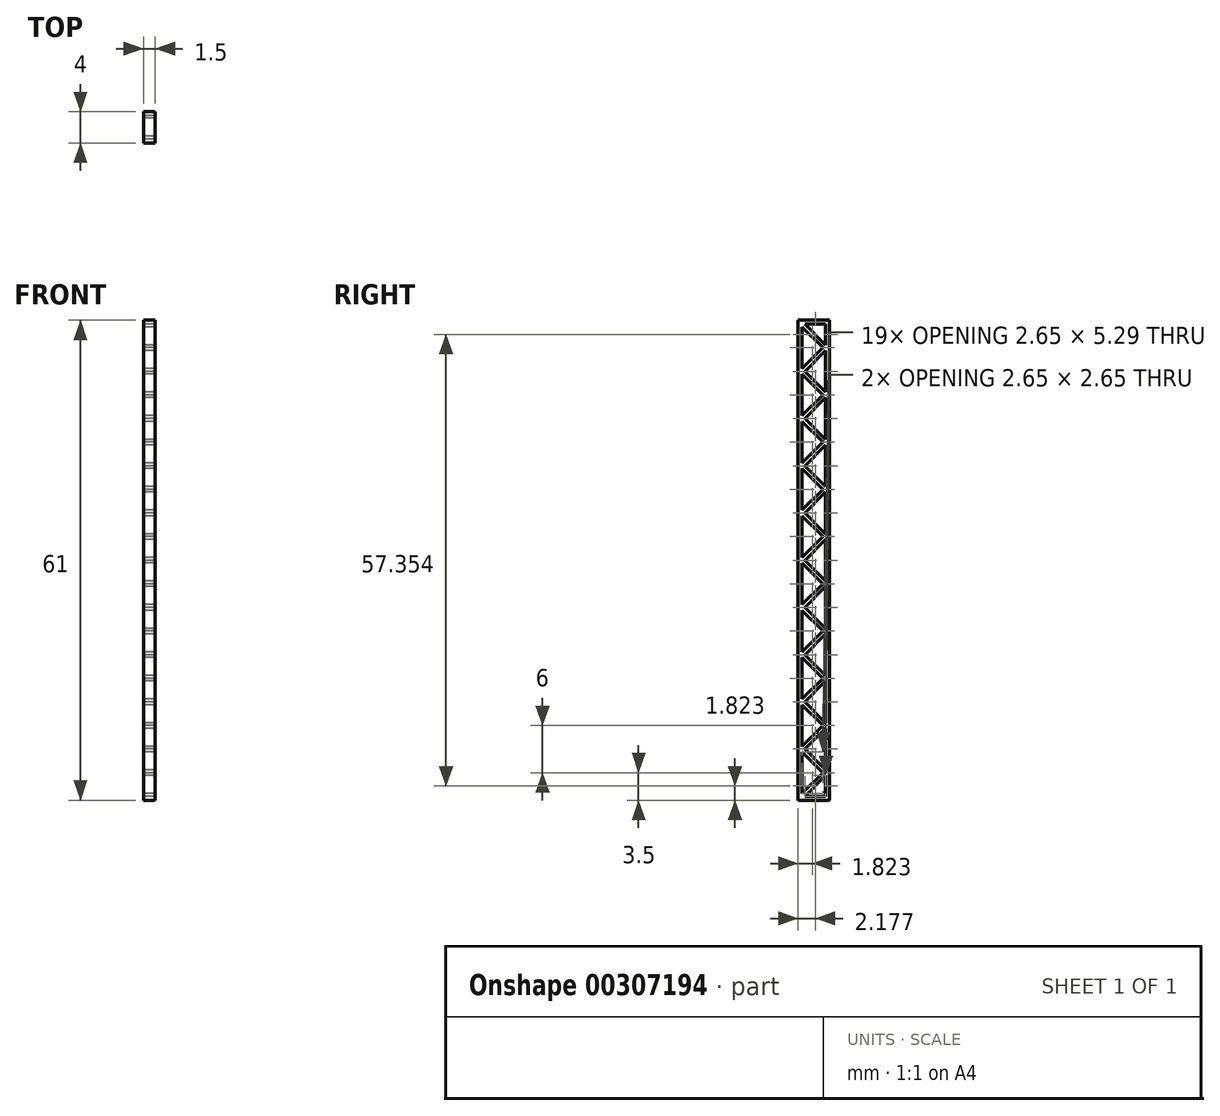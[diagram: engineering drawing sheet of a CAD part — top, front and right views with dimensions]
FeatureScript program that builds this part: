
annotation { "Feature Type Name" : "Feature", "Feature Type Description" : "" }
export const myFeature = defineFeature(function(context is Context, id is Id, definition is map)
    precondition{}
    {
        {
            var Q0;
            Q0=qCreatedBy(makeId("Right.planeOp"),FACE);
            var sketch = newSketch(context, id + "F0", { "sketchPlane" : qUnion([Q0])});
            skLineSegment(sketch, "E0.bottom", {"start": v(0, 0) * mm, "end": v(4, 0) * mm});
            skLineSegment(sketch, "E0.left", {"start": v(0, 0) * mm, "end": v(0, -60) * mm});
            skLineSegment(sketch, "E0.right", {"start": v(4, 0) * mm, "end": v(4, -60) * mm});
            skLineSegment(sketch, "E1.0", {"start": v(3.5, -0.5) * mm, "end": v(3.5, -3.15) * mm});
            skLineSegment(sketch, "E1.1", {"start": v(0.85, -0.5) * mm, "end": v(3.5, -0.5) * mm});
            skLineSegment(sketch, "E1.2", {"start": v(0.5, -0.85) * mm, "end": v(0.5, -6.15) * mm});
            skLineSegment(sketch, "E2.0", {"start": v(0.5, -0.85) * mm, "end": v(3.15, -3.5) * mm});
            skLineSegment(sketch, "E3.0", {"start": v(0.85, -0.5) * mm, "end": v(3.5, -3.15) * mm});
            skLineSegment(sketch, "E4.trimOffspring", {"start": v(3.5, -3.85) * mm, "end": v(3.5, -9.15) * mm});
            skLineSegment(sketch, "E5", {"start": v(3.15, -3.5) * mm, "end": v(0.5, -6.15) * mm});
            skLineSegment(sketch, "E6", {"start": v(0.85, -6.5) * mm, "end": v(3.5, -9.15) * mm});
            skLineSegment(sketch, "E7", {"start": v(3.15, -9.5) * mm, "end": v(0.5, -12.15) * mm});
            skLineSegment(sketch, "E8", {"start": v(0.85, -12.5) * mm, "end": v(3.5, -15.15) * mm});
            skLineSegment(sketch, "E9", {"start": v(3.15, -15.5) * mm, "end": v(0.5, -18.15) * mm});
            skLineSegment(sketch, "E10", {"start": v(0.85, -18.5) * mm, "end": v(3.5, -21.15) * mm});
            skLineSegment(sketch, "E11", {"start": v(3.15, -21.5) * mm, "end": v(0.5, -24.15) * mm});
            skLineSegment(sketch, "E12", {"start": v(0.85, -24.5) * mm, "end": v(3.5, -27.15) * mm});
            skLineSegment(sketch, "E13", {"start": v(3.15, -27.5) * mm, "end": v(0.5, -30.15) * mm});
            skLineSegment(sketch, "E14", {"start": v(0.85, -30.5) * mm, "end": v(3.5, -33.15) * mm});
            skLineSegment(sketch, "E15", {"start": v(3.15, -33.5) * mm, "end": v(0.5, -36.15) * mm});
            skLineSegment(sketch, "E16", {"start": v(0.85, -36.5) * mm, "end": v(3.5, -39.15) * mm});
            skLineSegment(sketch, "E17", {"start": v(3.15, -39.5) * mm, "end": v(0.5, -42.15) * mm});
            skLineSegment(sketch, "E18", {"start": v(0.85, -42.5) * mm, "end": v(3.5, -45.15) * mm});
            skLineSegment(sketch, "E19", {"start": v(3.15, -45.5) * mm, "end": v(0.5, -48.15) * mm});
            skLineSegment(sketch, "E20", {"start": v(0.85, -48.5) * mm, "end": v(3.5, -51.15) * mm});
            skLineSegment(sketch, "E21", {"start": v(3.15, -51.5) * mm, "end": v(0.5, -54.15) * mm});
            skLineSegment(sketch, "E22", {"start": v(0.85, -54.5) * mm, "end": v(3.5, -57.15) * mm});
            skLineSegment(sketch, "E23", {"start": v(3.15, -57.5) * mm, "end": v(0.5, -60.15) * mm});
            skLineSegment(sketch, "E24", {"start": v(3.5, -3.85) * mm, "end": v(0.85, -6.5) * mm});
            skLineSegment(sketch, "E25", {"start": v(0.5, -6.85) * mm, "end": v(3.15, -9.5) * mm});
            skLineSegment(sketch, "E26", {"start": v(3.5, -9.85) * mm, "end": v(0.85, -12.5) * mm});
            skLineSegment(sketch, "E27", {"start": v(0.5, -12.85) * mm, "end": v(3.15, -15.5) * mm});
            skLineSegment(sketch, "E28", {"start": v(3.5, -15.85) * mm, "end": v(0.85, -18.5) * mm});
            skLineSegment(sketch, "E29", {"start": v(0.5, -18.85) * mm, "end": v(3.15, -21.5) * mm});
            skLineSegment(sketch, "E30", {"start": v(3.5, -21.85) * mm, "end": v(0.85, -24.5) * mm});
            skLineSegment(sketch, "E31", {"start": v(0.5, -24.85) * mm, "end": v(3.15, -27.5) * mm});
            skLineSegment(sketch, "E32", {"start": v(3.5, -27.85) * mm, "end": v(0.85, -30.5) * mm});
            skLineSegment(sketch, "E33", {"start": v(0.5, -30.85) * mm, "end": v(3.15, -33.5) * mm});
            skLineSegment(sketch, "E34", {"start": v(3.5, -33.85) * mm, "end": v(0.85, -36.5) * mm});
            skLineSegment(sketch, "E35", {"start": v(0.5, -36.85) * mm, "end": v(3.15, -39.5) * mm});
            skLineSegment(sketch, "E36", {"start": v(3.5, -39.85) * mm, "end": v(0.85, -42.5) * mm});
            skLineSegment(sketch, "E37", {"start": v(0.5, -42.85) * mm, "end": v(3.15, -45.5) * mm});
            skLineSegment(sketch, "E38", {"start": v(3.5, -45.85) * mm, "end": v(0.85, -48.5) * mm});
            skLineSegment(sketch, "E39", {"start": v(0.5, -48.85) * mm, "end": v(3.15, -51.5) * mm});
            skLineSegment(sketch, "E40", {"start": v(3.5, -51.85) * mm, "end": v(0.85, -54.5) * mm});
            skLineSegment(sketch, "E41", {"start": v(0.5, -54.85) * mm, "end": v(3.15, -57.5) * mm});
            skLineSegment(sketch, "E42", {"start": v(3.5, -57.85) * mm, "end": v(0.85, -60.5) * mm});
            skLineSegment(sketch, "E43", {"start": v(0.35, -61) * mm, "end": v(4, -61) * mm});
            skLineSegment(sketch, "E44", {"start": v(4, -60) * mm, "end": v(4, -61) * mm});
            skLineSegment(sketch, "E45", {"start": v(0.35, -61) * mm, "end": v(0, -61) * mm});
            skLineSegment(sketch, "E46", {"start": v(0, -61) * mm, "end": v(0, -60) * mm});
            skPoint(sketch, "E47.orphan", {"position": v(0, -61.35) * mm});
            skLineSegment(sketch, "E48", {"start": v(0.5, -59.5) * mm, "end": v(0.5, -60.15) * mm});
            skLineSegment(sketch, "E49", {"start": v(3.5, -59.5) * mm, "end": v(3.5, -60.5) * mm});
            skLineSegment(sketch, "E50.1", {"start": v(0.85, -60.5) * mm, "end": v(3.5, -60.5) * mm});
            skLineSegment(sketch, "E51.trimOffspring", {"start": v(3.5, -57.85) * mm, "end": v(3.5, -59.5) * mm});
            skLineSegment(sketch, "E52.trimOffspring", {"start": v(0.5, -54.85) * mm, "end": v(0.5, -59.5) * mm});
            skLineSegment(sketch, "E53.trimOffspring", {"start": v(3.5, -51.85) * mm, "end": v(3.5, -57.15) * mm});
            skLineSegment(sketch, "E54.trimOffspring", {"start": v(3.5, -45.85) * mm, "end": v(3.5, -51.15) * mm});
            skLineSegment(sketch, "E55.trimOffspring", {"start": v(0.5, -48.85) * mm, "end": v(0.5, -54.15) * mm});
            skLineSegment(sketch, "E56.trimOffspring", {"start": v(3.5, -39.85) * mm, "end": v(3.5, -45.15) * mm});
            skLineSegment(sketch, "E57.trimOffspring", {"start": v(0.5, -42.85) * mm, "end": v(0.5, -48.15) * mm});
            skLineSegment(sketch, "E58.trimOffspring", {"start": v(3.5, -33.85) * mm, "end": v(3.5, -39.15) * mm});
            skLineSegment(sketch, "E59.trimOffspring", {"start": v(0.5, -36.85) * mm, "end": v(0.5, -42.15) * mm});
            skLineSegment(sketch, "E60.trimOffspring", {"start": v(3.5, -27.85) * mm, "end": v(3.5, -33.15) * mm});
            skLineSegment(sketch, "E61.trimOffspring", {"start": v(0.5, -30.85) * mm, "end": v(0.5, -36.15) * mm});
            skLineSegment(sketch, "E62.trimOffspring", {"start": v(0.5, -24.85) * mm, "end": v(0.5, -30.15) * mm});
            skLineSegment(sketch, "E63.trimOffspring", {"start": v(3.5, -21.85) * mm, "end": v(3.5, -27.15) * mm});
            skLineSegment(sketch, "E64.trimOffspring", {"start": v(3.5, -15.85) * mm, "end": v(3.5, -21.15) * mm});
            skLineSegment(sketch, "E65.trimOffspring", {"start": v(0.5, -18.85) * mm, "end": v(0.5, -24.15) * mm});
            skLineSegment(sketch, "E66.trimOffspring", {"start": v(0.5, -12.85) * mm, "end": v(0.5, -18.15) * mm});
            skLineSegment(sketch, "E67.trimOffspring", {"start": v(3.5, -9.85) * mm, "end": v(3.5, -15.15) * mm});
            skLineSegment(sketch, "E68.trimOffspring", {"start": v(0.5, -6.85) * mm, "end": v(0.5, -12.15) * mm});
            skSolve(sketch);
        }
        {
            var Q0;
            Q0 = qSketchRegion(id + "F0", true);
            extrude(context, id + "F1", {"entities" : qUnion([Q0]), "depth" : 1.5 * mm});
        }
    });
